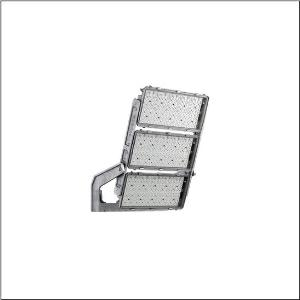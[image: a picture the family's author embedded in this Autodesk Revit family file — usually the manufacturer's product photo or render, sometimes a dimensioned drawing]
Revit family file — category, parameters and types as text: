
# Revit family: floodlight_fl_11_maxi_pro_remote___pl43_5xa779427a01ba_e28e
name_source: partatom
category: Lighting Fixtures
units: mm (PartAtom-declared; Revit-internal decimal feet)

## family parameters
Cut with Voids When Loaded = No
Host = Face
Light Source = No
Part Type = Normal
Room Calculation Point = No
Round Connector Dimension = Use Diameter
Shared = No

## types (1)
- --- (1 x LED, 151320 lm, 1095.9 W, 5000K)
    Apparent Load = 1096 VA
    CIE Flux Codes = 25 74 99 100 100
    Color Rendering = 70
    Color Temperature = 5000K
    Default Elevation = 1800 mm
    Description = Floodlight FL 11  maxi  pro Remote floodlight; light control with lens of PMMA; cover panel of toughened safety glass, transparent; light distribution: PL43, asymmetric direct distribution, LEDcolour temperature: 5000K, rated luminous flux: 151.320lm, colour rendering: CRI > 70, light colour: 750; luminous efficacy: 138lm/W; brightness control: DALI 2 (1 DALI address); with terminal, 8-pole, max. 2.5mm², mains connection: 220..240V/380..400V AC, 50/60Hz, surge voltage resistance: line to ground: 10kV, ECG replaceable separately, no afterglow with DALI off / DMX off command, LED unit replaceable without ESD environment, dustproof LED module, dimming range 10..100%; 1096W floodlight with 2x LED unit of diecast aluminium, coated grey; length: 713mm / width: 651mm / height: 338mm; mounting bracket, of diecast aluminium, uncoated, natural, equipment: Power, protection rating (complete): IP66; insulation class (complete): insulation class I (protective earthing); certification: CE, ENEC, VDE; ball protection: ball impact resistance with accessories, impact resistance: IK07; only for outdoor installations, rated ambient temperature 10°C, permissible operating ambient temperature: -40..+30°C, permissible storage temperature: -40..+85°C; packaging unit: 1 piece

Light Distribution: PL43
    Height = 320 mm
    Lamp = 1 x LED
    Lamp Light Flux = 151320 lm
    Lamp Power = 1095.9 W
    Lamp count = 1
    Length = 1002 mm
    Luminous efficacy = 138 lm/W
    Manufacturer = Siteco
    ModVariant = No
    Model = 5XA779427A01BA
    Mounting Place = Ceiling
    Mounting Type = Surface mounted
    Number of Poles = 1
    OnlyDefault = Yes
    Power Factor = 1
    Product Name = Floodlight FL 11 maxi pro Remote | PL43
    Product group = floodlight | ceiling mounted
    ProductGroupID = 302
    Protection Class = Protection class I
    Protection Degree = IP 66
    RLX_Detail_Level = 1
    RLX_Emergency_Light_Flux = 0 lm
    RLX_Emergency_Type = 0
    RLX_Emergency_Type_DB = No
    RlxData = <blob elided: 52529 chars, md5=050be231>
    Socket = socket
    Standby Power = 0 W
    System Light Flux = 151320 lm
    System Power = 1096 W
    Type Comments = factory setting: luminous flux: 100 % | dim-lin: 254 | 760 mA
    Type Image = l_1006784.jpg
    URL = http://relux.com
    VarID = @adj_065149
    Voltage = 0 V
    Weight = 0.00 kg
    Width = 655 mm

## geometry (parser evidence)
native form markers: Blend x4, Sweep x12
no freeform markers — native parametric forms only
